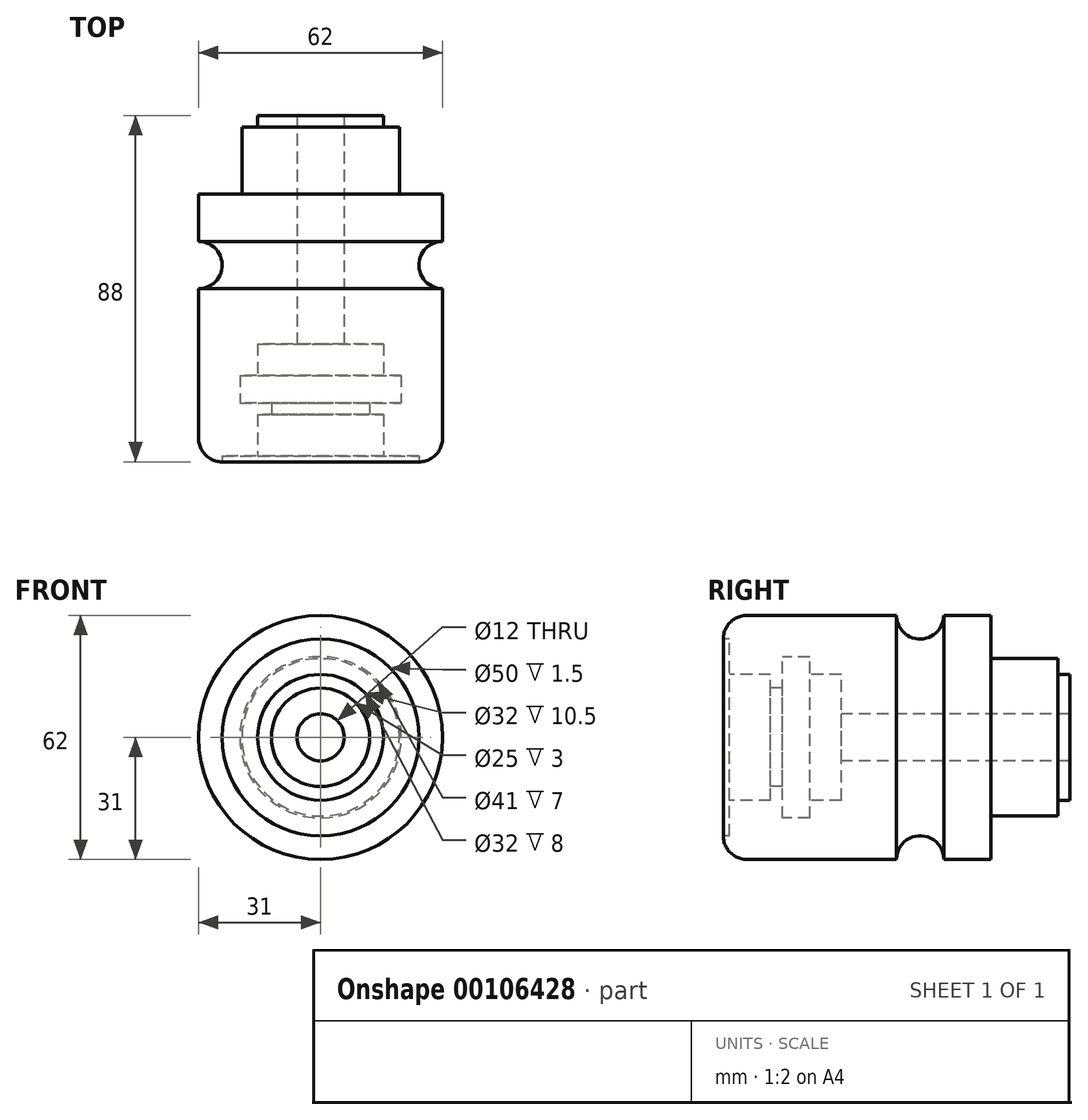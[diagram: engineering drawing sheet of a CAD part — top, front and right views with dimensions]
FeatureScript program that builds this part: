
annotation { "Feature Type Name" : "Feature", "Feature Type Description" : "" }
export const myFeature = defineFeature(function(context is Context, id is Id, definition is map)
    precondition{}
    {
        {
            var Q0;
            Q0=qCreatedBy(makeId("Right.planeOp"),FACE);
            var sketch = newSketch(context, id + "F0", { "sketchPlane" : qUnion([Q0])});
            skLineSegment(sketch, "E0", {"start": v(0, 0) * mm, "end": v(88, 0) * mm});
            skLineSegment(sketch, "E1", {"start": v(88, 0) * mm, "end": v(88, 16) * mm});
            skLineSegment(sketch, "E2", {"start": v(88, 16) * mm, "end": v(85, 16) * mm});
            skLineSegment(sketch, "E3", {"start": v(85, 16) * mm, "end": v(85, 20) * mm});
            skLineSegment(sketch, "E4", {"start": v(85, 20) * mm, "end": v(68, 20) * mm});
            skLineSegment(sketch, "E5", {"start": v(68, 20) * mm, "end": v(68, 31) * mm});
            skLineSegment(sketch, "E6", {"start": v(68, 31) * mm, "end": v(56, 31) * mm});
            skLineSegment(sketch, "E7", {"start": v(44, 31) * mm, "end": v(6, 31) * mm});
            skLineSegment(sketch, "E8", {"start": v(0, 25) * mm, "end": v(0, 0) * mm});
            skLineSegment(sketch, "E9", {"start": v(88, 6) * mm, "end": v(30, 6) * mm});
            skLineSegment(sketch, "E10", {"start": v(30, 6) * mm, "end": v(30, 16) * mm});
            skLineSegment(sketch, "E11", {"start": v(30, 16) * mm, "end": v(22, 16) * mm});
            skLineSegment(sketch, "E12", {"start": v(22, 16) * mm, "end": v(22, 20.5) * mm});
            skLineSegment(sketch, "E13", {"start": v(22, 20.5) * mm, "end": v(15, 20.5) * mm});
            skLineSegment(sketch, "E14", {"start": v(15, 20.5) * mm, "end": v(15, 12.5) * mm});
            skLineSegment(sketch, "E15", {"start": v(15, 12.5) * mm, "end": v(12, 12.5) * mm});
            skLineSegment(sketch, "E16", {"start": v(12, 12.5) * mm, "end": v(12, 16) * mm});
            skLineSegment(sketch, "E17", {"start": v(12, 16) * mm, "end": v(1.5, 16) * mm});
            skLineSegment(sketch, "E18", {"start": v(1.5, 16) * mm, "end": v(1.5, 25) * mm});
            skLineSegment(sketch, "E19", {"start": v(1.5, 25) * mm, "end": v(0, 25) * mm});
            skArc(sketch, "E20", {"start": v(44, 31) * mm, "mid": v(50, 25) * mm, "end": v(56, 31) * mm});
            skPoint(sketch, "E21.visualSharp", {"position": v(0, 31) * mm});
            skArc(sketch, "E21.filletArc", {"start": v(6, 31) * mm, "mid": v(1.76, 29.24) * mm, "end": v(0, 25) * mm});
            skSolve(sketch);
        }
        {
            var Q0;
            {var subQ4=sQuery(id+"F0.wireOp",EDGE,"E2");Q0=makeQuery(id+"F0.imprint","IMPRINT",FACE,{"disambiguationData":[TD([[makeQuery(id+"F0.imprint","IMPRINT",EDGE,{"derivedFrom":subQ4}),1.0]])]});}
            var Q1;
            Q1=sQuery(id+"F0.wireOp",EDGE,"E0");
            revolve(context, id + "F1", {"entities" : qUnion([Q0]), "axis" : qUnion([Q1]), "revolveType" : RevolveType.FULL});
        }
    });
